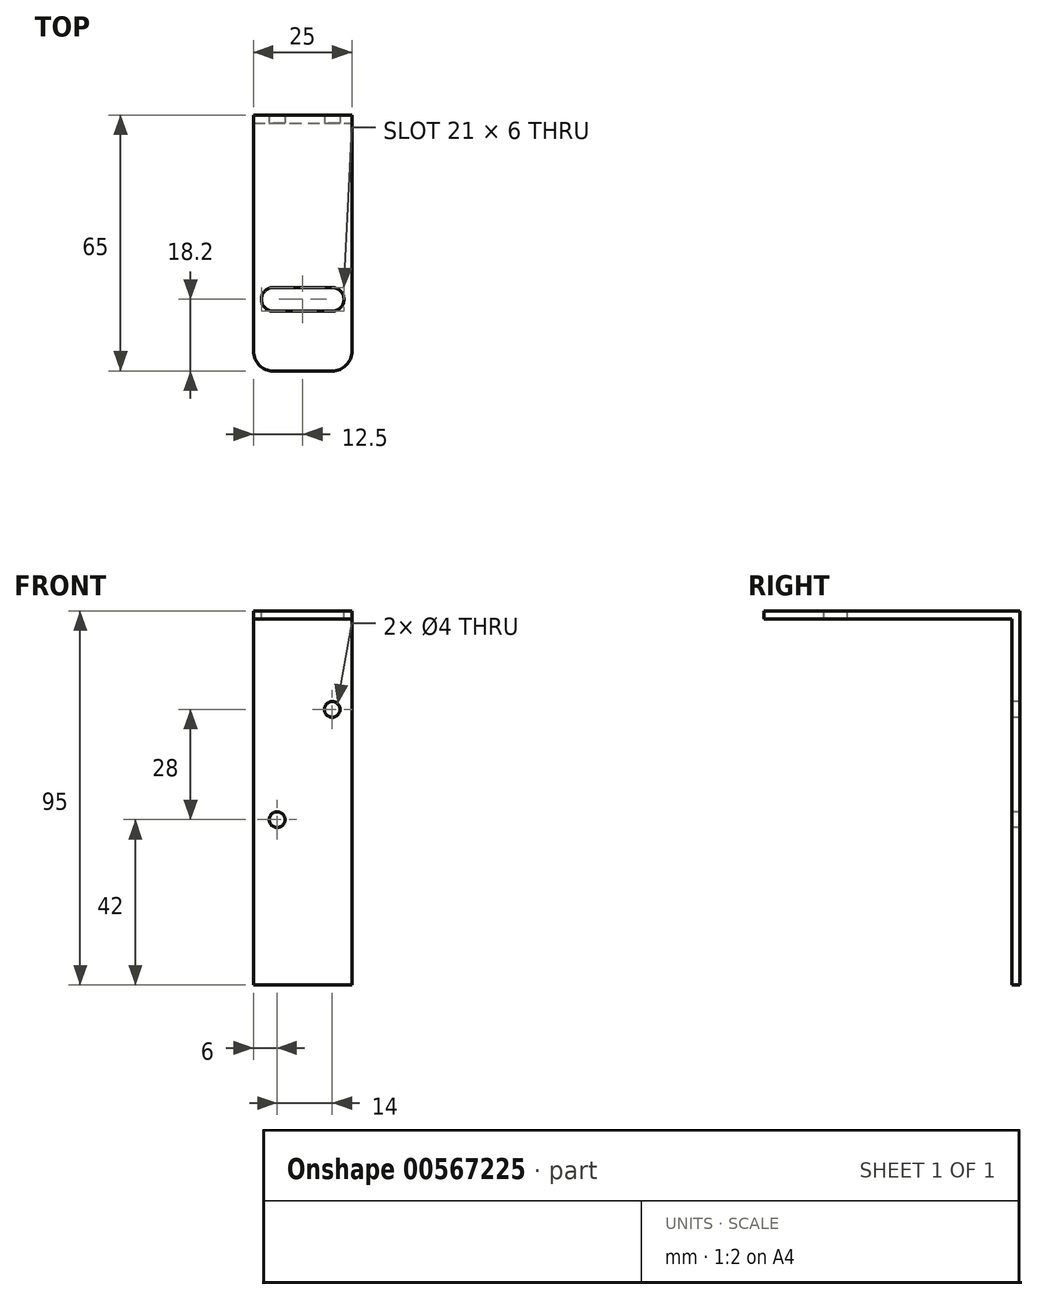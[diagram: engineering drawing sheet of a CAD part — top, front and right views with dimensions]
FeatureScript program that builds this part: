
annotation { "Feature Type Name" : "Feature", "Feature Type Description" : "" }
export const myFeature = defineFeature(function(context is Context, id is Id, definition is map)
    precondition{}
    {
        {
            var Q0;
            Q0=qCreatedBy(makeId("Front.planeOp"),FACE);
            var sketch = newSketch(context, id + "F0", { "sketchPlane" : qUnion([Q0])});
            skLineSegment(sketch, "E0.bottom", {"start": v(-12.5, 45) * mm, "end": v(12.5, 45) * mm});
            skLineSegment(sketch, "E0.top", {"start": v(-12.5, -45) * mm, "end": v(12.5, -45) * mm});
            skLineSegment(sketch, "E0.left", {"start": v(-12.5, 45) * mm, "end": v(-12.5, -45) * mm});
            skLineSegment(sketch, "E0.right", {"start": v(12.5, 45) * mm, "end": v(12.5, -45) * mm});
            skPoint(sketch, "E0.middle", {"position": v(0, 0) * mm});
            skSolve(sketch);
        }
        {
            var Q0;
            Q0=makeQuery(id+"F0.imprint","IMPRINT",FACE,{"disambiguationData":[TD([[makeQuery(id+"F0.imprint","IMPRINT",EDGE,{"derivedFrom":sQuery(id+"F0.wireOp",EDGE,"E0.bottom")}),-1.0]])]});
            extrude(context, id + "F1", {"entities" : qUnion([Q0]), "depth" : 2 * mm, "offsetDistance" : 25 * mm});
        }
        {
            var Q0;
            Q0=makeQuery(id+"F1.opExtrude","CAP_FACE",FACE,{"disambiguationData":[OSD([sQuery(id+"F0.wireOp",EDGE,"E0.bottom"),sQuery(id+"F0.wireOp",EDGE,"E0.top"),sQuery(id+"F0.wireOp",EDGE,"E0.left"),sQuery(id+"F0.wireOp",EDGE,"E0.right")])],"isStart":false});
            var sketch = newSketch(context, id + "F2", { "sketchPlane" : qUnion([Q0])});
            skCircle(sketch, "E1", {"center": v(7.5, 25) * mm, "radius": 2 * mm});
            skCircle(sketch, "E2", {"center": v(-6.5, -3) * mm, "radius": 2 * mm});
            skSolve(sketch);
        }
        {
            var Q0;
            Q0=qSketchRegion(id+"F2",true);
            extrude(context, id + "F3", {"entities" : qUnion([Q0]), "operationType" : NewBodyOperationType.REMOVE, "oppositeDirection" : true, "depth" : 25 * mm, "offsetDistance" : 25 * mm});
        }
        {
            var Q0;
            Q0=makeQuery(id+"F1.opExtrude","CAP_FACE",FACE,{"disambiguationData":[OSD([sQuery(id+"F0.wireOp",EDGE,"E0.bottom"),sQuery(id+"F0.wireOp",EDGE,"E0.top"),sQuery(id+"F0.wireOp",EDGE,"E0.left"),sQuery(id+"F0.wireOp",EDGE,"E0.right")])],"isStart":false});
            var sketch = newSketch(context, id + "F4", { "sketchPlane" : qUnion([Q0])});
            skLineSegment(sketch, "E3.bottom", {"start": v(-12.5, 45) * mm, "end": v(12.5, 45) * mm});
            skLineSegment(sketch, "E4", {"start": v(12.5, 45) * mm, "end": v(12.5, 50) * mm});
            skLineSegment(sketch, "E5", {"start": v(12.5, 50) * mm, "end": v(-12.5, 50) * mm});
            skLineSegment(sketch, "E6", {"start": v(-12.5, 50) * mm, "end": v(-12.5, 45) * mm});
            skSolve(sketch);
        }
        {
            var Q0;
            Q0=makeQuery(id+"F4.imprint","IMPRINT",FACE,{"disambiguationData":[TD([[makeQuery(id+"F4.imprint","IMPRINT",EDGE,{"derivedFrom":sQuery(id+"F4.wireOp",EDGE,"E3.bottom")}),1.0]])]});
            extrude(context, id + "F5", {"entities" : qUnion([Q0]), "operationType" : NewBodyOperationType.ADD, "oppositeDirection" : true, "depth" : 2 * mm, "offsetDistance" : 25 * mm});
        }
        {
            var Q0;
            Q0=makeQuery(id+"F5.boolean.opBoolean","MERGE",FACE,{"derivedFrom":[makeQuery(id+"F1.opExtrude","CAP_FACE",FACE,{"disambiguationData":[OSD([sQuery(id+"F0.wireOp",EDGE,"E0.bottom"),sQuery(id+"F0.wireOp",EDGE,"E0.top"),sQuery(id+"F0.wireOp",EDGE,"E0.left"),sQuery(id+"F0.wireOp",EDGE,"E0.right")])],"isStart":false}),makeQuery(id+"F5.opExtrude","CAP_FACE",FACE,{"disambiguationData":[OSD([sQuery(id+"F4.wireOp",EDGE,"E3.bottom"),sQuery(id+"F4.wireOp",EDGE,"E4"),sQuery(id+"F4.wireOp",EDGE,"E5"),sQuery(id+"F4.wireOp",EDGE,"E6")])],"isStart":true})]});
            var sketch = newSketch(context, id + "F6", { "sketchPlane" : qUnion([Q0])});
            skLineSegment(sketch, "E7.bottom", {"start": v(-12.5, 50) * mm, "end": v(12.5, 50) * mm});
            skLineSegment(sketch, "E7.top", {"start": v(-12.5, 48) * mm, "end": v(12.5, 48) * mm});
            skLineSegment(sketch, "E7.left", {"start": v(-12.5, 50) * mm, "end": v(-12.5, 48) * mm});
            skLineSegment(sketch, "E7.right", {"start": v(12.5, 50) * mm, "end": v(12.5, 48) * mm});
            skSolve(sketch);
        }
        {
            var Q0;
            Q0 = qSketchRegion(id + "F6", true);
            extrude(context, id + "F7", {"entities" : qUnion([Q0]), "operationType" : NewBodyOperationType.ADD, "depth" : 63 * mm, "offsetDistance" : 25 * mm});
        }
        {
            var Q0;
            Q0=makeQuery(id+"F7.opExtrude","CAP_EDGE",EDGE,{"disambiguationData":[OSD([sQuery(id+"F6.wireOp",EDGE,"E7.left")])],"isStart":false});
            var Q1;
            Q1=makeQuery(id+"F7.opExtrude","CAP_EDGE",EDGE,{"disambiguationData":[OSD([sQuery(id+"F6.wireOp",EDGE,"E7.right")])],"isStart":false});
            fillet(context, id + "F8", {"entities" : qUnion([Q0, Q1]), "radius" : 5 * mm, "tangentPropagation" : true, "allowEdgeOverflow" : false});
        }
        {
            var Q0;
            Q0=makeQuery(id+"F7.boolean.opBoolean","MERGE",FACE,{"derivedFrom":[makeQuery(id+"F5.opExtrude","SWEPT_FACE",FACE,{"disambiguationData":[OSD([sQuery(id+"F4.wireOp",EDGE,"E5")])]}),makeQuery(id+"F7.opExtrude","SWEPT_FACE",FACE,{"disambiguationData":[OSD([sQuery(id+"F6.wireOp",EDGE,"E7.bottom")])]})]});
            var sketch = newSketch(context, id + "F9", { "sketchPlane" : qUnion([Q0])});
            skArc(sketch, "E8", {"start": v(7.5, -49.8) * mm, "mid": v(10.5, -46.8) * mm, "end": v(7.5, -43.8) * mm});
            skArc(sketch, "E9", {"start": v(-7.5, -43.8) * mm, "mid": v(-10.5, -46.8) * mm, "end": v(-7.5, -49.8) * mm});
            skLineSegment(sketch, "E10", {"start": v(-7.5, -49.8) * mm, "end": v(7.5, -49.8) * mm});
            skLineSegment(sketch, "E11", {"start": v(-7.5, -43.8) * mm, "end": v(7.5, -43.8) * mm});
            skSolve(sketch);
        }
        {
            var Q0;
            Q0 = qSketchRegion(id + "F9", true);
            extrude(context, id + "F10", {"entities" : qUnion([Q0]), "operationType" : NewBodyOperationType.REMOVE, "oppositeDirection" : true, "depth" : 25 * mm, "offsetDistance" : 25 * mm});
        }
    });
